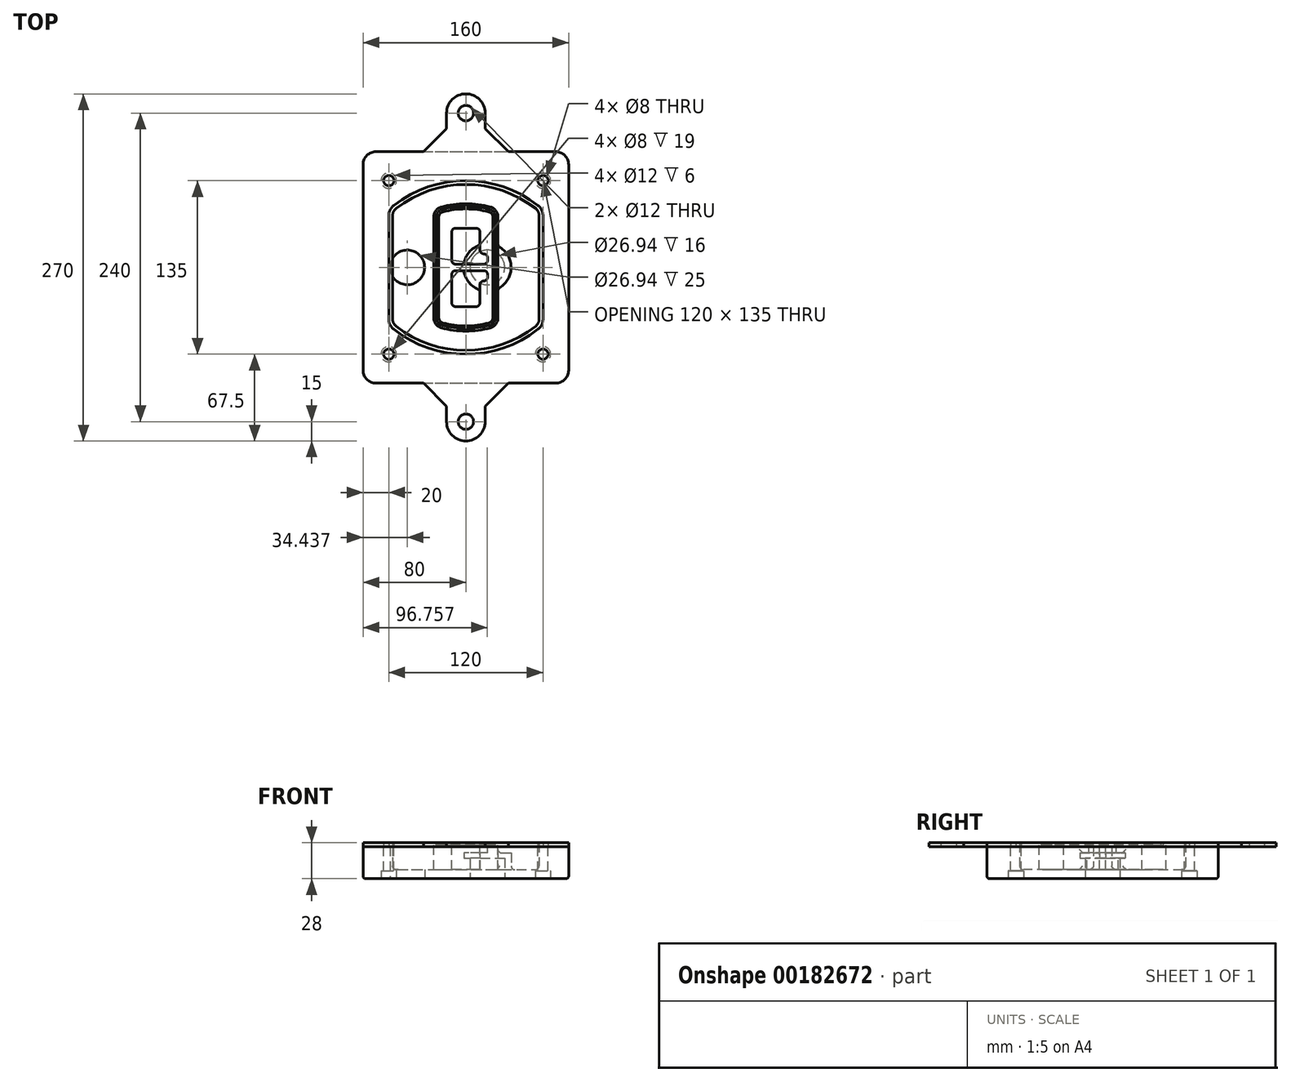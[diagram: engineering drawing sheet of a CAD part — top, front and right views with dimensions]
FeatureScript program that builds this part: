
annotation { "Feature Type Name" : "Feature", "Feature Type Description" : "" }
export const myFeature = defineFeature(function(context is Context, id is Id, definition is map)
    precondition{}
    {
        {
            var Q0;
            Q0=qCreatedBy(makeId("Top.planeOp"),FACE);
            var sketch = newSketch(context, id + "F0", { "sketchPlane" : qUnion([Q0])});
            skPoint(sketch, "E0.rect.middle", {"position": v(0, 0) * mm});
            skLineSegment(sketch, "E1.bottom", {"start": v(-70, -90) * mm, "end": v(70, -90) * mm});
            skLineSegment(sketch, "E1.top", {"start": v(-70, 90) * mm, "end": v(70, 90) * mm});
            skLineSegment(sketch, "E1.left", {"start": v(-80, -80) * mm, "end": v(-80, 80) * mm});
            skLineSegment(sketch, "E1.right", {"start": v(80, -80) * mm, "end": v(80, 80) * mm});
            skLineSegment(sketch, "E2", {"start": v(-80, 90) * mm, "end": v(80, -90) * mm, "construction": true});
            skLineSegment(sketch, "E3", {"start": v(80, 90) * mm, "end": v(-80, -90) * mm, "construction": true});
            skCircle(sketch, "E4", {"center": v(-60, 67.5) * mm, "radius": 4 * mm});
            skCircle(sketch, "E5", {"center": v(60, 67.5) * mm, "radius": 4 * mm});
            skCircle(sketch, "E6", {"center": v(60, -67.5) * mm, "radius": 4 * mm});
            skCircle(sketch, "E7", {"center": v(-60, -67.5) * mm, "radius": 4 * mm});
            skLineSegment(sketch, "E8", {"start": v(-60, 67.5) * mm, "end": v(60, 67.5) * mm, "construction": true});
            skLineSegment(sketch, "E9", {"start": v(60, 67.5) * mm, "end": v(60, -67.5) * mm, "construction": true});
            skLineSegment(sketch, "E10", {"start": v(60, -67.5) * mm, "end": v(-60, -67.5) * mm, "construction": true});
            skLineSegment(sketch, "E11", {"start": v(-60, -67.5) * mm, "end": v(-60, 67.5) * mm, "construction": true});
            skLineSegment(sketch, "E12", {"start": v(-60, 40.3) * mm, "end": v(-60, -40.3) * mm});
            skLineSegment(sketch, "E13", {"start": v(60, 40.3) * mm, "end": v(60, -40.3) * mm});
            skArc(sketch, "E14", {"start": v(56.15, 48.18) * mm, "mid": v(0, 67.5) * mm, "end": v(-56.15, 48.18) * mm});
            skArc(sketch, "E15", {"start": v(-56.15, -48.18) * mm, "mid": v(0, -67.5) * mm, "end": v(56.15, -48.18) * mm});
            skLineSegment(sketch, "E16", {"start": v(-60, 0) * mm, "end": v(60, 0) * mm, "construction": true});
            skPoint(sketch, "E17.visualSharp", {"position": v(-60, -45) * mm});
            skArc(sketch, "E17.filletArc", {"start": v(-60, -40.3) * mm, "mid": v(-58.99, -44.68) * mm, "end": v(-56.15, -48.18) * mm});
            skPoint(sketch, "E18.visualSharp", {"position": v(-60, 45) * mm});
            skArc(sketch, "E18.filletArc", {"start": v(-56.15, 48.18) * mm, "mid": v(-58.99, 44.68) * mm, "end": v(-60, 40.3) * mm});
            skPoint(sketch, "E19.visualSharp", {"position": v(60, 45) * mm});
            skArc(sketch, "E19.filletArc", {"start": v(60, 40.3) * mm, "mid": v(58.99, 44.68) * mm, "end": v(56.15, 48.18) * mm});
            skPoint(sketch, "E20.visualSharp", {"position": v(60, -45) * mm});
            skArc(sketch, "E20.filletArc", {"start": v(56.15, -48.18) * mm, "mid": v(58.99, -44.68) * mm, "end": v(60, -40.3) * mm});
            skPoint(sketch, "E21.visualSharp", {"position": v(-80, 90) * mm});
            skArc(sketch, "E21.filletArc", {"start": v(-70, 90) * mm, "mid": v(-77.07, 87.07) * mm, "end": v(-80, 80) * mm});
            skPoint(sketch, "E22.visualSharp", {"position": v(80, 90) * mm});
            skArc(sketch, "E22.filletArc", {"start": v(80, 80) * mm, "mid": v(77.07, 87.07) * mm, "end": v(70, 90) * mm});
            skPoint(sketch, "E23.visualSharp", {"position": v(80, -90) * mm});
            skArc(sketch, "E23.filletArc", {"start": v(70, -90) * mm, "mid": v(77.07, -87.07) * mm, "end": v(80, -80) * mm});
            skPoint(sketch, "E24.visualSharp", {"position": v(-80, -90) * mm});
            skArc(sketch, "E24.filletArc", {"start": v(-80, -80) * mm, "mid": v(-77.07, -87.07) * mm, "end": v(-70, -90) * mm});
            skArc(sketch, "E25.0", {"start": v(57, 40.3) * mm, "mid": v(56.3, 43.36) * mm, "end": v(54.3, 45.81) * mm});
            skLineSegment(sketch, "E25.1", {"start": v(57, 40.3) * mm, "end": v(57, -40.3) * mm});
            skArc(sketch, "E25.2", {"start": v(54.3, -45.81) * mm, "mid": v(56.3, -43.36) * mm, "end": v(57, -40.3) * mm});
            skArc(sketch, "E25.3", {"start": v(-54.3, -45.81) * mm, "mid": v(0, -64.5) * mm, "end": v(54.3, -45.81) * mm});
            skArc(sketch, "E25.4", {"start": v(-57, -40.3) * mm, "mid": v(-56.3, -43.36) * mm, "end": v(-54.3, -45.81) * mm});
            skArc(sketch, "E25.5", {"start": v(54.3, 45.81) * mm, "mid": v(0, 64.5) * mm, "end": v(-54.3, 45.81) * mm});
            skLineSegment(sketch, "E25.6", {"start": v(-57, 40.3) * mm, "end": v(-57, -40.3) * mm});
            skArc(sketch, "E25.7", {"start": v(-54.3, 45.81) * mm, "mid": v(-56.3, 43.36) * mm, "end": v(-57, 40.3) * mm});
            skArc(sketch, "E26.0", {"start": v(-58.62, 51.33) * mm, "mid": v(-62.58, 46.43) * mm, "end": v(-64, 40.3) * mm});
            skArc(sketch, "E26.1", {"start": v(58.62, 51.33) * mm, "mid": v(0, 71.5) * mm, "end": v(-58.62, 51.33) * mm});
            skArc(sketch, "E26.2", {"start": v(64, 40.3) * mm, "mid": v(62.58, 46.43) * mm, "end": v(58.62, 51.33) * mm});
            skLineSegment(sketch, "E26.3", {"start": v(64, 40.3) * mm, "end": v(64, -40.3) * mm});
            skArc(sketch, "E26.4", {"start": v(58.62, -51.33) * mm, "mid": v(62.58, -46.43) * mm, "end": v(64, -40.3) * mm});
            skLineSegment(sketch, "E26.5", {"start": v(-64, 40.3) * mm, "end": v(-64, -40.3) * mm});
            skArc(sketch, "E26.6", {"start": v(-58.62, -51.33) * mm, "mid": v(0, -71.5) * mm, "end": v(58.62, -51.33) * mm});
            skArc(sketch, "E26.7", {"start": v(-64, -40.3) * mm, "mid": v(-62.58, -46.43) * mm, "end": v(-58.62, -51.33) * mm});
            skSolve(sketch);
        }
        {
            var Q0;
            Q0=makeQuery(id+"F0.imprint","IMPRINT",FACE,{"disambiguationData":[TD([[makeQuery(id+"F0.imprint","IMPRINT",EDGE,{"derivedFrom":sQuery(id+"F0.wireOp",EDGE,"E1.bottom")}),1.0]])]});
            var Q1;
            Q1=makeQuery(id+"F0.imprint","IMPRINT",FACE,{"disambiguationData":[TD([[makeQuery(id+"F0.imprint","IMPRINT",EDGE,{"derivedFrom":sQuery(id+"F0.wireOp",EDGE,"E12")}),1.0]])]});
            var Q2;
            Q2=makeQuery(id+"F0.imprint","IMPRINT",FACE,{"disambiguationData":[TD([[makeQuery(id+"F0.imprint","IMPRINT",EDGE,{"derivedFrom":sQuery(id+"F0.wireOp",EDGE,"E25.0")}),1.0]])]});
            var Q3;
            Q3=makeQuery(id+"F0.imprint","IMPRINT",FACE,{"disambiguationData":[TD([[makeQuery(id+"F0.imprint","IMPRINT",EDGE,{"derivedFrom":sQuery(id+"F0.wireOp",EDGE,"E12")}),-1.0]])]});
            extrude(context, id + "F1", {"entities" : qUnion([Q0, Q1, Q2, Q3]), "oppositeDirection" : true, "depth" : 25 * mm});
        }
        {
            var Q0;
            Q0=makeQuery(id+"F0.imprint","IMPRINT",FACE,{"disambiguationData":[TD([[makeQuery(id+"F0.imprint","IMPRINT",EDGE,{"derivedFrom":sQuery(id+"F0.wireOp",EDGE,"E12")}),1.0]])]});
            extrude(context, id + "F2", {"entities" : qUnion([Q0]), "operationType" : NewBodyOperationType.ADD, "depth" : 3 * mm});
        }
        {
            var Q0;
            Q0=makeQuery(id+"F0.imprint","IMPRINT",FACE,{"disambiguationData":[TD([[makeQuery(id+"F0.imprint","IMPRINT",EDGE,{"derivedFrom":sQuery(id+"F0.wireOp",EDGE,"E25.0")}),1.0]])]});
            extrude(context, id + "F3", {"entities" : qUnion([Q0]), "operationType" : NewBodyOperationType.REMOVE, "oppositeDirection" : true, "depth" : 18 * mm});
        }
        {
            var Q0;
            Q0=makeQuery(id+"F2.opExtrude","CAP_FACE",FACE,{"disambiguationData":[OSD([sQuery(id+"F0.wireOp",EDGE,"E12"),sQuery(id+"F0.wireOp",EDGE,"E13"),sQuery(id+"F0.wireOp",EDGE,"E14"),sQuery(id+"F0.wireOp",EDGE,"E15"),sQuery(id+"F0.wireOp",EDGE,"E17.filletArc"),sQuery(id+"F0.wireOp",EDGE,"E18.filletArc"),sQuery(id+"F0.wireOp",EDGE,"E19.filletArc"),sQuery(id+"F0.wireOp",EDGE,"E20.filletArc"),sQuery(id+"F0.wireOp",EDGE,"E25.0"),sQuery(id+"F0.wireOp",EDGE,"E25.1"),sQuery(id+"F0.wireOp",EDGE,"E25.2"),sQuery(id+"F0.wireOp",EDGE,"E25.3"),sQuery(id+"F0.wireOp",EDGE,"E25.4"),sQuery(id+"F0.wireOp",EDGE,"E25.5"),sQuery(id+"F0.wireOp",EDGE,"E25.6"),sQuery(id+"F0.wireOp",EDGE,"E25.7")])],"isStart":false});
            var sketch = newSketch(context, id + "F4", { "sketchPlane" : qUnion([Q0])});
            skArc(sketch, "E27.0", {"start": v(-19.08, -46.97) * mm, "mid": v(0, -49.5) * mm, "end": v(19.08, -46.97) * mm});
            skArc(sketch, "E28.0", {"start": v(19.08, 46.97) * mm, "mid": v(0, 49.5) * mm, "end": v(-19.08, 46.97) * mm});
            skLineSegment(sketch, "E29", {"start": v(-25, 39.25) * mm, "end": v(-25, -39.25) * mm});
            skLineSegment(sketch, "E30", {"start": v(25, 39.25) * mm, "end": v(25, -39.25) * mm});
            skLineSegment(sketch, "E31", {"start": v(-25, 45.1) * mm, "end": v(25, 45.1) * mm, "construction": true});
            skLineSegment(sketch, "E32", {"start": v(-25, -45.1) * mm, "end": v(25, -45.1) * mm, "construction": true});
            skPoint(sketch, "E33.visualSharp", {"position": v(-25, 45.1) * mm});
            skArc(sketch, "E33.filletArc", {"start": v(-19.08, 46.97) * mm, "mid": v(-23.35, 44.11) * mm, "end": v(-25, 39.25) * mm});
            skPoint(sketch, "E34.visualSharp", {"position": v(25, 45.1) * mm});
            skArc(sketch, "E34.filletArc", {"start": v(25, 39.25) * mm, "mid": v(23.35, 44.11) * mm, "end": v(19.08, 46.97) * mm});
            skPoint(sketch, "E35.visualSharp", {"position": v(25, -45.1) * mm});
            skArc(sketch, "E35.filletArc", {"start": v(19.08, -46.97) * mm, "mid": v(23.35, -44.11) * mm, "end": v(25, -39.25) * mm});
            skPoint(sketch, "E36.visualSharp", {"position": v(-25, -45.1) * mm});
            skArc(sketch, "E36.filletArc", {"start": v(-25, -39.25) * mm, "mid": v(-23.35, -44.11) * mm, "end": v(-19.08, -46.97) * mm});
            skArc(sketch, "E37.0", {"start": v(54.3, 45.81) * mm, "mid": v(0, 64.5) * mm, "end": v(-54.3, 45.81) * mm});
            skArc(sketch, "E37.1", {"start": v(-54.3, 45.81) * mm, "mid": v(-56.3, 43.36) * mm, "end": v(-57, 40.3) * mm});
            skLineSegment(sketch, "E37.2", {"start": v(-57, 40.3) * mm, "end": v(-57, -40.3) * mm});
            skArc(sketch, "E37.3", {"start": v(-57, -40.3) * mm, "mid": v(-56.3, -43.36) * mm, "end": v(-54.3, -45.81) * mm});
            skArc(sketch, "E37.4", {"start": v(-54.3, -45.81) * mm, "mid": v(0, -64.5) * mm, "end": v(54.3, -45.81) * mm});
            skArc(sketch, "E37.5", {"start": v(54.3, -45.81) * mm, "mid": v(56.3, -43.36) * mm, "end": v(57, -40.3) * mm});
            skLineSegment(sketch, "E37.6", {"start": v(57, 40.3) * mm, "end": v(57, -40.3) * mm});
            skArc(sketch, "E37.7", {"start": v(57, 40.3) * mm, "mid": v(56.3, 43.36) * mm, "end": v(54.3, 45.81) * mm});
            skLineSegment(sketch, "E38.0", {"start": v(23, 39.25) * mm, "end": v(23, -39.25) * mm});
            skArc(sketch, "E38.1", {"start": v(18.56, -45.04) * mm, "mid": v(21.76, -42.9) * mm, "end": v(23, -39.25) * mm});
            skArc(sketch, "E38.2", {"start": v(-18.56, -45.04) * mm, "mid": v(0, -47.5) * mm, "end": v(18.56, -45.04) * mm});
            skArc(sketch, "E38.3", {"start": v(-23, -39.25) * mm, "mid": v(-21.76, -42.9) * mm, "end": v(-18.56, -45.04) * mm});
            skLineSegment(sketch, "E38.4", {"start": v(-23, 39.25) * mm, "end": v(-23, -39.25) * mm});
            skArc(sketch, "E38.5", {"start": v(23, 39.25) * mm, "mid": v(21.76, 42.9) * mm, "end": v(18.56, 45.04) * mm});
            skArc(sketch, "E38.6", {"start": v(-18.56, 45.04) * mm, "mid": v(-21.76, 42.9) * mm, "end": v(-23, 39.25) * mm});
            skArc(sketch, "E38.7", {"start": v(18.56, 45.04) * mm, "mid": v(0, 47.5) * mm, "end": v(-18.56, 45.04) * mm});
            skArc(sketch, "E39.0", {"start": v(21, 39.25) * mm, "mid": v(20.18, 41.68) * mm, "end": v(18.04, 43.1) * mm});
            skLineSegment(sketch, "E39.1", {"start": v(21, 39.25) * mm, "end": v(21, -39.25) * mm});
            skArc(sketch, "E39.2", {"start": v(18.04, -43.1) * mm, "mid": v(20.18, -41.68) * mm, "end": v(21, -39.25) * mm});
            skArc(sketch, "E39.3", {"start": v(-18.04, -43.1) * mm, "mid": v(0, -45.5) * mm, "end": v(18.04, -43.1) * mm});
            skArc(sketch, "E39.4", {"start": v(-21, -39.25) * mm, "mid": v(-20.18, -41.68) * mm, "end": v(-18.04, -43.1) * mm});
            skArc(sketch, "E39.5", {"start": v(18.04, 43.1) * mm, "mid": v(0, 45.5) * mm, "end": v(-18.04, 43.1) * mm});
            skLineSegment(sketch, "E39.6", {"start": v(-21, 39.25) * mm, "end": v(-21, -39.25) * mm});
            skArc(sketch, "E39.7", {"start": v(-18.04, 43.1) * mm, "mid": v(-20.18, 41.68) * mm, "end": v(-21, 39.25) * mm});
            skLineSegment(sketch, "E40", {"start": v(-25, 0) * mm, "end": v(25, 0) * mm, "construction": true});
            skLineSegment(sketch, "E41", {"start": v(-11, 5.5) * mm, "end": v(-11, 27.5) * mm});
            skLineSegment(sketch, "E42", {"start": v(-8, 30.5) * mm, "end": v(8, 30.5) * mm});
            skLineSegment(sketch, "E43", {"start": v(11, 27.5) * mm, "end": v(11, 13.5) * mm});
            skLineSegment(sketch, "E44", {"start": v(14, 10.5) * mm, "end": v(14, 10.5) * mm});
            skLineSegment(sketch, "E45", {"start": v(17, 7.5) * mm, "end": v(17, 5.5) * mm});
            skLineSegment(sketch, "E46", {"start": v(14, 2.5) * mm, "end": v(-8, 2.5) * mm});
            skPoint(sketch, "E47.visualSharp", {"position": v(-11, 30.5) * mm});
            skArc(sketch, "E47.filletArc", {"start": v(-8, 30.5) * mm, "mid": v(-10.12, 29.62) * mm, "end": v(-11, 27.5) * mm});
            skPoint(sketch, "E48.visualSharp", {"position": v(11, 30.5) * mm});
            skArc(sketch, "E48.filletArc", {"start": v(11, 27.5) * mm, "mid": v(10.12, 29.62) * mm, "end": v(8, 30.5) * mm});
            skPoint(sketch, "E49.visualSharp", {"position": v(11, 10.5) * mm});
            skArc(sketch, "E49.filletArc", {"start": v(11, 13.5) * mm, "mid": v(11.88, 11.38) * mm, "end": v(14, 10.5) * mm});
            skPoint(sketch, "E50.visualSharp", {"position": v(17, 10.5) * mm});
            skArc(sketch, "E50.filletArc", {"start": v(17, 7.5) * mm, "mid": v(16.12, 9.62) * mm, "end": v(14, 10.5) * mm});
            skPoint(sketch, "E51.visualSharp", {"position": v(17, 2.5) * mm});
            skArc(sketch, "E51.filletArc", {"start": v(14, 2.5) * mm, "mid": v(16.12, 3.38) * mm, "end": v(17, 5.5) * mm});
            skPoint(sketch, "E52.visualSharp", {"position": v(-11, 2.5) * mm});
            skArc(sketch, "E52.filletArc", {"start": v(-11, 5.5) * mm, "mid": v(-10.12, 3.38) * mm, "end": v(-8, 2.5) * mm});
            skLineSegment(sketch, "E53.0.MirrorCS", {"start": v(14, -2.5) * mm, "end": v(-8, -2.5) * mm});
            skArc(sketch, "E54.0.MirrorCS", {"start": v(-11, -5.5) * mm, "mid": v(-10.12, -3.38) * mm, "end": v(-8, -2.5) * mm});
            skLineSegment(sketch, "E55.0.MirrorCS", {"start": v(-11, -5.5) * mm, "end": v(-11, -27.5) * mm});
            skArc(sketch, "E56.0.MirrorCS", {"start": v(-8, -30.5) * mm, "mid": v(-10.12, -29.62) * mm, "end": v(-11, -27.5) * mm});
            skLineSegment(sketch, "E57.0.MirrorCS", {"start": v(-8, -30.5) * mm, "end": v(8, -30.5) * mm});
            skArc(sketch, "E58.0.MirrorCS", {"start": v(11, -27.5) * mm, "mid": v(10.12, -29.62) * mm, "end": v(8, -30.5) * mm});
            skLineSegment(sketch, "E59.0.MirrorCS", {"start": v(11, -27.5) * mm, "end": v(11, -13.5) * mm});
            skArc(sketch, "E60.0.MirrorCS", {"start": v(11, -13.5) * mm, "mid": v(11.88, -11.38) * mm, "end": v(14, -10.5) * mm});
            skArc(sketch, "E61.0.MirrorCS", {"start": v(17, -7.5) * mm, "mid": v(16.12, -9.62) * mm, "end": v(14, -10.5) * mm});
            skLineSegment(sketch, "E62.0.MirrorCS", {"start": v(17, -7.5) * mm, "end": v(17, -5.5) * mm});
            skArc(sketch, "E63.0.MirrorCS", {"start": v(14, -2.5) * mm, "mid": v(16.12, -3.38) * mm, "end": v(17, -5.5) * mm});
            skSolve(sketch);
        }
        {
            var Q0;
            Q0=makeQuery(id+"F4.imprint","IMPRINT",FACE,{"disambiguationData":[TD([[makeQuery(id+"F4.imprint","IMPRINT",EDGE,{"derivedFrom":sQuery(id+"F4.wireOp",EDGE,"E27.0")}),1.0]])]});
            var Q1;
            Q1=makeQuery(id+"F4.imprint","IMPRINT",FACE,{"disambiguationData":[TD([[makeQuery(id+"F4.imprint","IMPRINT",EDGE,{"derivedFrom":sQuery(id+"F4.wireOp",EDGE,"E38.0")}),-1.0]])]});
            var Q2;
            Q2=makeQuery(id+"F4.imprint","IMPRINT",FACE,{"disambiguationData":[TD([[makeQuery(id+"F4.imprint","IMPRINT",EDGE,{"derivedFrom":sQuery(id+"F4.wireOp",EDGE,"E39.0")}),1.0]])]});
            extrude(context, id + "F5", {"entities" : qUnion([Q0, Q1, Q2]), "operationType" : NewBodyOperationType.ADD, "endBound" : BoundingType.UP_TO_NEXT, "oppositeDirection" : true, "depth" : 25 * mm});
        }
        {
            var Q0;
            Q0=makeQuery(id+"F4.imprint","IMPRINT",FACE,{"disambiguationData":[TD([[makeQuery(id+"F4.imprint","IMPRINT",EDGE,{"derivedFrom":sQuery(id+"F4.wireOp",EDGE,"E38.0")}),-1.0]])]});
            extrude(context, id + "F6", {"entities" : qUnion([Q0]), "operationType" : NewBodyOperationType.REMOVE, "oppositeDirection" : true, "depth" : 2 * mm});
        }
        {
            var Q0;
            Q0=makeQuery(id+"F1.opExtrude","CAP_FACE",FACE,{"disambiguationData":[OSD([sQuery(id+"F0.wireOp",EDGE,"E1.bottom"),sQuery(id+"F0.wireOp",EDGE,"E1.top"),sQuery(id+"F0.wireOp",EDGE,"E1.left"),sQuery(id+"F0.wireOp",EDGE,"E1.right"),sQuery(id+"F0.wireOp",EDGE,"E4"),sQuery(id+"F0.wireOp",EDGE,"E5"),sQuery(id+"F0.wireOp",EDGE,"E6"),sQuery(id+"F0.wireOp",EDGE,"E7"),sQuery(id+"F0.wireOp",EDGE,"E21.filletArc"),sQuery(id+"F0.wireOp",EDGE,"E22.filletArc"),sQuery(id+"F0.wireOp",EDGE,"E23.filletArc"),sQuery(id+"F0.wireOp",EDGE,"E24.filletArc")])],"isStart":false});
            var sketch = newSketch(context, id + "F7", { "sketchPlane" : qUnion([Q0])});
            skCircle(sketch, "E64", {"center": v(16.76, 0) * mm, "radius": 13.47 * mm});
            skCircle(sketch, "E65", {"center": v(-45.56, 0) * mm, "radius": 13.47 * mm});
            skLineSegment(sketch, "E66", {"start": v(80, 0) * mm, "end": v(-80, 0) * mm});
            skCircle(sketch, "E67", {"center": v(16.76, 0) * mm, "radius": 18.47 * mm});
            skCircle(sketch, "E68", {"center": v(60, -67.5) * mm, "radius": 6 * mm});
            skCircle(sketch, "E69", {"center": v(-60, -67.5) * mm, "radius": 6 * mm});
            skCircle(sketch, "E70", {"center": v(-60, 67.5) * mm, "radius": 6 * mm});
            skCircle(sketch, "E71", {"center": v(60, 67.5) * mm, "radius": 6 * mm});
            skSolve(sketch);
        }
        {
            var Q0;
            {var subQ1=sQuery(id+"F7.wireOp",EDGE,"E66");var subQ4=sQuery(id+"F7.wireOp",EDGE,"E64");var subQ6=makeQuery(id+"F7.imprint","INTERSECT",VERTEX,{"disambiguationData":[OD(0.0)],"derivedFrom":[subQ4,subQ1]});Q0=makeQuery(id+"F7.imprint","IMPRINT",FACE,{"disambiguationData":[TD([[makeQuery(id+"F7.imprint","IMPRINT",EDGE,{"disambiguationData":[TD([[subQ6,-1.0]])],"derivedFrom":subQ4}),-1.0]])]});}
            var Q1;
            {var subQ0=sQuery(id+"F7.wireOp",EDGE,"E66");var subQ1=sQuery(id+"F7.wireOp",EDGE,"E64");var subQ3=makeQuery(id+"F7.imprint","INTERSECT",VERTEX,{"disambiguationData":[OD(0.0)],"derivedFrom":[subQ1,subQ0]});Q1=makeQuery(id+"F7.imprint","IMPRINT",FACE,{"disambiguationData":[TD([[makeQuery(id+"F7.imprint","IMPRINT",EDGE,{"disambiguationData":[TD([[subQ3,-1.0]])],"derivedFrom":subQ1}),1.0]])]});}
            var Q2;
            {var subQ0=sQuery(id+"F7.wireOp",EDGE,"E66");var subQ1=sQuery(id+"F7.wireOp",EDGE,"E64");var subQ3=makeQuery(id+"F7.imprint","INTERSECT",VERTEX,{"disambiguationData":[OD(0.0)],"derivedFrom":[subQ1,subQ0]});Q2=makeQuery(id+"F7.imprint","IMPRINT",FACE,{"disambiguationData":[TD([[makeQuery(id+"F7.imprint","IMPRINT",EDGE,{"disambiguationData":[TD([[subQ3,1.0]])],"derivedFrom":subQ1}),1.0]])]});}
            var Q3;
            {var subQ1=sQuery(id+"F7.wireOp",EDGE,"E66");var subQ4=sQuery(id+"F7.wireOp",EDGE,"E64");var subQ6=makeQuery(id+"F7.imprint","INTERSECT",VERTEX,{"disambiguationData":[OD(0.0)],"derivedFrom":[subQ4,subQ1]});Q3=makeQuery(id+"F7.imprint","IMPRINT",FACE,{"disambiguationData":[TD([[makeQuery(id+"F7.imprint","IMPRINT",EDGE,{"disambiguationData":[TD([[subQ6,1.0]])],"derivedFrom":subQ4}),-1.0]])]});}
            extrude(context, id + "F8", {"entities" : qUnion([Q0, Q1, Q2, Q3]), "operationType" : NewBodyOperationType.ADD, "oppositeDirection" : true, "depth" : 20 * mm});
        }
        {
            var Q0;
            {var subQ0=sQuery(id+"F7.wireOp",EDGE,"E66");var subQ1=sQuery(id+"F7.wireOp",EDGE,"E64");var subQ3=makeQuery(id+"F7.imprint","INTERSECT",VERTEX,{"disambiguationData":[OD(0.0)],"derivedFrom":[subQ1,subQ0]});Q0=makeQuery(id+"F7.imprint","IMPRINT",FACE,{"disambiguationData":[TD([[makeQuery(id+"F7.imprint","IMPRINT",EDGE,{"disambiguationData":[TD([[subQ3,-1.0]])],"derivedFrom":subQ1}),1.0]])]});}
            var Q1;
            {var subQ0=sQuery(id+"F7.wireOp",EDGE,"E66");var subQ1=sQuery(id+"F7.wireOp",EDGE,"E64");var subQ3=makeQuery(id+"F7.imprint","INTERSECT",VERTEX,{"disambiguationData":[OD(0.0)],"derivedFrom":[subQ1,subQ0]});Q1=makeQuery(id+"F7.imprint","IMPRINT",FACE,{"disambiguationData":[TD([[makeQuery(id+"F7.imprint","IMPRINT",EDGE,{"disambiguationData":[TD([[subQ3,1.0]])],"derivedFrom":subQ1}),1.0]])]});}
            extrude(context, id + "F9", {"entities" : qUnion([Q0, Q1]), "operationType" : NewBodyOperationType.REMOVE, "oppositeDirection" : true, "depth" : 16 * mm});
        }
        {
            var Q0;
            {var subQ0=sQuery(id+"F7.wireOp",EDGE,"E66");var subQ1=sQuery(id+"F7.wireOp",EDGE,"E65");var subQ3=makeQuery(id+"F7.imprint","INTERSECT",VERTEX,{"disambiguationData":[OD(0.0)],"derivedFrom":[subQ1,subQ0]});Q0=makeQuery(id+"F7.imprint","IMPRINT",FACE,{"disambiguationData":[TD([[makeQuery(id+"F7.imprint","IMPRINT",EDGE,{"disambiguationData":[TD([[subQ3,-1.0]])],"derivedFrom":subQ1}),1.0]])]});}
            var Q1;
            {var subQ0=sQuery(id+"F7.wireOp",EDGE,"E66");var subQ1=sQuery(id+"F7.wireOp",EDGE,"E65");var subQ3=makeQuery(id+"F7.imprint","INTERSECT",VERTEX,{"disambiguationData":[OD(0.0)],"derivedFrom":[subQ1,subQ0]});Q1=makeQuery(id+"F7.imprint","IMPRINT",FACE,{"disambiguationData":[TD([[makeQuery(id+"F7.imprint","IMPRINT",EDGE,{"disambiguationData":[TD([[subQ3,1.0]])],"derivedFrom":subQ1}),1.0]])]});}
            extrude(context, id + "F10", {"entities" : qUnion([Q0, Q1]), "operationType" : NewBodyOperationType.REMOVE, "oppositeDirection" : true, "depth" : 25 * mm});
        }
        {
            var Q0;
            Q0=makeQuery(id+"F7.imprint","IMPRINT",FACE,{"disambiguationData":[TD([[makeQuery(id+"F7.imprint","IMPRINT",EDGE,{"derivedFrom":sQuery(id+"F7.wireOp",EDGE,"E68")}),1.0]])]});
            var Q1;
            Q1=makeQuery(id+"F7.imprint","IMPRINT",FACE,{"disambiguationData":[TD([[makeQuery(id+"F7.imprint","IMPRINT",EDGE,{"derivedFrom":makeQuery(id+"F1.opExtrude","CAP_EDGE",EDGE,{"disambiguationData":[OSD([sQuery(id+"F0.wireOp",EDGE,"E5")])],"isStart":false})}),-1.0]])]});
            var Q2;
            Q2=makeQuery(id+"F7.imprint","IMPRINT",FACE,{"disambiguationData":[TD([[makeQuery(id+"F7.imprint","IMPRINT",EDGE,{"derivedFrom":sQuery(id+"F7.wireOp",EDGE,"E69")}),1.0]])]});
            var Q3;
            Q3=makeQuery(id+"F7.imprint","IMPRINT",FACE,{"disambiguationData":[TD([[makeQuery(id+"F7.imprint","IMPRINT",EDGE,{"derivedFrom":makeQuery(id+"F1.opExtrude","CAP_EDGE",EDGE,{"disambiguationData":[OSD([sQuery(id+"F0.wireOp",EDGE,"E4")])],"isStart":false})}),-1.0]])]});
            var Q4;
            Q4=makeQuery(id+"F7.imprint","IMPRINT",FACE,{"disambiguationData":[TD([[makeQuery(id+"F7.imprint","IMPRINT",EDGE,{"derivedFrom":sQuery(id+"F7.wireOp",EDGE,"E70")}),1.0]])]});
            var Q5;
            Q5=makeQuery(id+"F7.imprint","IMPRINT",FACE,{"disambiguationData":[TD([[makeQuery(id+"F7.imprint","IMPRINT",EDGE,{"derivedFrom":makeQuery(id+"F1.opExtrude","CAP_EDGE",EDGE,{"disambiguationData":[OSD([sQuery(id+"F0.wireOp",EDGE,"E7")])],"isStart":false})}),-1.0]])]});
            var Q6;
            Q6=makeQuery(id+"F7.imprint","IMPRINT",FACE,{"disambiguationData":[TD([[makeQuery(id+"F7.imprint","IMPRINT",EDGE,{"derivedFrom":sQuery(id+"F7.wireOp",EDGE,"E71")}),1.0]])]});
            var Q7;
            Q7=makeQuery(id+"F7.imprint","IMPRINT",FACE,{"disambiguationData":[TD([[makeQuery(id+"F7.imprint","IMPRINT",EDGE,{"derivedFrom":makeQuery(id+"F1.opExtrude","CAP_EDGE",EDGE,{"disambiguationData":[OSD([sQuery(id+"F0.wireOp",EDGE,"E6")])],"isStart":false})}),-1.0]])]});
            extrude(context, id + "F11", {"entities" : qUnion([Q0, Q1, Q2, Q3, Q4, Q5, Q6, Q7]), "operationType" : NewBodyOperationType.REMOVE, "oppositeDirection" : true, "depth" : 6 * mm});
        }
        {
            var Q0;
            Q0=makeQuery(id+"F9.boolean.opBoolean","COPY",FACE,{"derivedFrom":makeQuery(id+"F9.opExtrude","CAP_FACE",FACE,{"disambiguationData":[OSD([sQuery(id+"F7.wireOp",EDGE,"E64")])],"isStart":false})});
            var sketch = newSketch(context, id + "F12", { "sketchPlane" : qUnion([Q0])});
            skArc(sketch, "E72.0", {"start": v(11, 17.55) * mm, "mid": v(2.57, 11.82) * mm, "end": v(-1.54, 2.5) * mm});
            skArc(sketch, "E72.1", {"start": v(-1.54, -2.5) * mm, "mid": v(2.57, -11.82) * mm, "end": v(11, -17.55) * mm});
            skLineSegment(sketch, "E73", {"start": v(-1.54, -2.5) * mm, "end": v(14, -2.5) * mm});
            skLineSegment(sketch, "E74.0", {"start": v(14, 2.5) * mm, "end": v(-1.54, 2.5) * mm});
            skArc(sketch, "E74.1", {"start": v(14, 2.5) * mm, "mid": v(16.12, 3.38) * mm, "end": v(17, 5.5) * mm});
            skLineSegment(sketch, "E74.2", {"start": v(17, 7.5) * mm, "end": v(17, 5.5) * mm});
            skArc(sketch, "E74.3", {"start": v(17, 7.5) * mm, "mid": v(16.12, 9.62) * mm, "end": v(14, 10.5) * mm});
            skArc(sketch, "E74.4", {"start": v(11, 13.5) * mm, "mid": v(11.88, 11.38) * mm, "end": v(14, 10.5) * mm});
            skLineSegment(sketch, "E74.5", {"start": v(11, 17.55) * mm, "end": v(11, 13.5) * mm});
            skLineSegment(sketch, "E74.7", {"start": v(14, -2.5) * mm, "end": v(-1.54, -2.5) * mm});
            skArc(sketch, "E74.8", {"start": v(14, -2.5) * mm, "mid": v(16.12, -3.38) * mm, "end": v(17, -5.5) * mm});
            skLineSegment(sketch, "E74.9", {"start": v(17, -7.5) * mm, "end": v(17, -5.5) * mm});
            skArc(sketch, "E74.10", {"start": v(17, -7.5) * mm, "mid": v(16.12, -9.62) * mm, "end": v(14, -10.5) * mm});
            skArc(sketch, "E74.11", {"start": v(11, -13.5) * mm, "mid": v(11.88, -11.38) * mm, "end": v(14, -10.5) * mm});
            skLineSegment(sketch, "E74.12", {"start": v(11, -17.55) * mm, "end": v(11, -13.5) * mm});
            skPoint(sketch, "E75.orphan", {"position": v(11, -27.5) * mm});
            skPoint(sketch, "E76.orphan", {"position": v(-8, -2.5) * mm});
            skPoint(sketch, "E77.orphan", {"position": v(-8, 2.5) * mm});
            skPoint(sketch, "E78.orphan", {"position": v(11, 27.5) * mm});
            skSolve(sketch);
        }
        {
            var Q0;
            {var subQ7=sQuery(id+"F12.wireOp",EDGE,"E72.0");var subQ14=sQuery(id+"F12.wireOp",EDGE,"E72.1");var subQ16=sQuery(id+"F12.wireOp",EDGE,"E74.1");var subQ18=sQuery(id+"F12.wireOp",EDGE,"E74.8");Q0=qUnion([makeQuery(id+"F12.imprint","IMPRINT",FACE,{"disambiguationData":[TD([[makeQuery(id+"F12.imprint","IMPRINT",EDGE,{"derivedFrom":subQ7}),1.0]])]}),makeQuery(id+"F12.imprint","IMPRINT",FACE,{"disambiguationData":[TD([[makeQuery(id+"F12.imprint","IMPRINT",EDGE,{"derivedFrom":subQ14}),1.0]])]}),makeQuery(id+"F12.imprint","IMPRINT",FACE,{"disambiguationData":[TD([[makeQuery(id+"F12.imprint","IMPRINT",EDGE,{"derivedFrom":subQ16}),1.0]])]}),makeQuery(id+"F12.imprint","IMPRINT",FACE,{"disambiguationData":[TD([[makeQuery(id+"F12.imprint","IMPRINT",EDGE,{"derivedFrom":subQ18}),-1.0]])]})]);}
            var Q1;
            Q1=makeQuery(id+"F5.boolean.opBoolean","SPLIT",FACE,{"disambiguationData":[TD([makeQuery(id+"F5.opExtrude","SWEPT_FACE",FACE,{"disambiguationData":[OSD([sQuery(id+"F4.wireOp",EDGE,"E41")])]})])],"derivedFrom":makeQuery(id+"F3.boolean.opBoolean","COPY",FACE,{"derivedFrom":makeQuery(id+"F3.opExtrude","CAP_FACE",FACE,{"disambiguationData":[OSD([sQuery(id+"F0.wireOp",EDGE,"E25.0"),sQuery(id+"F0.wireOp",EDGE,"E25.1"),sQuery(id+"F0.wireOp",EDGE,"E25.2"),sQuery(id+"F0.wireOp",EDGE,"E25.3"),sQuery(id+"F0.wireOp",EDGE,"E25.4"),sQuery(id+"F0.wireOp",EDGE,"E25.5"),sQuery(id+"F0.wireOp",EDGE,"E25.6"),sQuery(id+"F0.wireOp",EDGE,"E25.7")])],"isStart":false})})});
            extrude(context, id + "F13", {"entities" : qUnion([Q0]), "operationType" : NewBodyOperationType.REMOVE, "endBound" : BoundingType.UP_TO_SURFACE, "endBoundEntityFace" : qUnion([Q1]), "depth" : 25 * mm});
        }
        {
            var Q0;
            Q0=makeQuery(id+"F3.boolean.opBoolean","COPY",EDGE,{"derivedFrom":makeQuery(id+"F3.opExtrude","CAP_EDGE",EDGE,{"disambiguationData":[OSD([sQuery(id+"F0.wireOp",EDGE,"E25.6")])],"isStart":false})});
            var Q1;
            Q1=makeQuery(id+"F8.boolean.opBoolean","INTERSECT",EDGE,{"derivedFrom":[makeQuery(id+"F5.opExtrude","SWEPT_FACE",FACE,{"disambiguationData":[OSD([sQuery(id+"F4.wireOp",EDGE,"E30")])]}),makeQuery(id+"F8.opExtrude","CAP_FACE",FACE,{"disambiguationData":[OSD([sQuery(id+"F7.wireOp",EDGE,"E67")])],"isStart":false})]});
            var Q2;
            Q2=makeQuery(id+"F8.boolean.opBoolean","INTERSECT",EDGE,{"disambiguationData":[OD(1.0)],"derivedFrom":[makeQuery(id+"F5.opExtrude","SWEPT_FACE",FACE,{"disambiguationData":[OSD([sQuery(id+"F4.wireOp",EDGE,"E30")])]}),makeQuery(id+"F8.opExtrude","SWEPT_FACE",FACE,{"disambiguationData":[OSD([sQuery(id+"F7.wireOp",EDGE,"E67")])]})]});
            var Q3;
            {var subQ0=sQuery(id+"F4.wireOp",EDGE,"E30");Q3=makeQuery(id+"F8.boolean.opBoolean","SPLIT",EDGE,{"disambiguationData":[TD([makeQuery(id+"F5.opExtrude","SWEPT_FACE",FACE,{"disambiguationData":[OSD([sQuery(id+"F4.wireOp",EDGE,"E35.filletArc")])]})])],"derivedFrom":makeQuery(id+"F5.opExtrude","CAP_EDGE",EDGE,{"disambiguationData":[OSD([subQ0])],"isStart":false})});}
            var Q4;
            {var subQ0=sQuery(id+"F0.wireOp",EDGE,"E25.7");var subQ1=sQuery(id+"F0.wireOp",EDGE,"E25.1");var subQ2=sQuery(id+"F0.wireOp",EDGE,"E25.6");var subQ3=sQuery(id+"F0.wireOp",EDGE,"E25.5");var subQ4=sQuery(id+"F0.wireOp",EDGE,"E25.4");var subQ5=sQuery(id+"F0.wireOp",EDGE,"E25.0");var subQ6=sQuery(id+"F0.wireOp",EDGE,"E25.2");var subQ7=sQuery(id+"F0.wireOp",EDGE,"E25.3");Q4=makeQuery(id+"F8.boolean.opBoolean","INTERSECT",EDGE,{"derivedFrom":[makeQuery(id+"F5.boolean.opBoolean","SPLIT",FACE,{"disambiguationData":[TD([makeQuery(id+"F2.opExtrude","SWEPT_FACE",FACE,{"disambiguationData":[OSD([subQ5])]})])],"derivedFrom":makeQuery(id+"F3.boolean.opBoolean","COPY",FACE,{"derivedFrom":makeQuery(id+"F3.opExtrude","CAP_FACE",FACE,{"disambiguationData":[OSD([subQ5,subQ1,subQ6,subQ7,subQ4,subQ3,subQ2,subQ0])],"isStart":false})})}),makeQuery(id+"F8.opExtrude","SWEPT_FACE",FACE,{"disambiguationData":[OSD([sQuery(id+"F7.wireOp",EDGE,"E67")])]})]});}
            var Q5;
            Q5=makeQuery(id+"F8.boolean.opBoolean","INTERSECT",EDGE,{"disambiguationData":[OD(0.0)],"derivedFrom":[makeQuery(id+"F5.opExtrude","SWEPT_FACE",FACE,{"disambiguationData":[OSD([sQuery(id+"F4.wireOp",EDGE,"E30")])]}),makeQuery(id+"F8.opExtrude","SWEPT_FACE",FACE,{"disambiguationData":[OSD([sQuery(id+"F7.wireOp",EDGE,"E67")])]})]});
            fillet(context, id + "F14", {"entities" : qUnion([Q0, Q1, Q2, Q3, Q4, Q5]), "radius" : 3 * mm, "tangentPropagation" : true, "allowEdgeOverflow" : false});
        }
        {
            var Q0;
            Q0=makeQuery(id+"F1.opExtrude","CAP_EDGE",EDGE,{"disambiguationData":[OSD([sQuery(id+"F0.wireOp",EDGE,"E1.bottom")])],"isStart":false});
            fillet(context, id + "F15", {"entities" : qUnion([Q0]), "radius" : 2 * mm, "tangentPropagation" : true, "allowEdgeOverflow" : false});
        }
        {
            var Q0;
            {var subQ0=sQuery(id+"F0.wireOp",EDGE,"E22.filletArc");var subQ1=sQuery(id+"F0.wireOp",EDGE,"E7");var subQ2=sQuery(id+"F0.wireOp",EDGE,"E6");var subQ3=sQuery(id+"F0.wireOp",EDGE,"E5");var subQ4=sQuery(id+"F0.wireOp",EDGE,"E4");var subQ5=sQuery(id+"F0.wireOp",EDGE,"E1.bottom");var subQ6=sQuery(id+"F0.wireOp",EDGE,"E21.filletArc");var subQ7=sQuery(id+"F0.wireOp",EDGE,"E1.top");var subQ8=sQuery(id+"F0.wireOp",EDGE,"E1.left");var subQ9=sQuery(id+"F0.wireOp",EDGE,"E1.right");var subQ10=sQuery(id+"F0.wireOp",EDGE,"E23.filletArc");var subQ11=sQuery(id+"F0.wireOp",EDGE,"E24.filletArc");Q0=makeQuery(id+"F2.boolean.opBoolean","SPLIT",FACE,{"disambiguationData":[TD([makeQuery(id+"F1.opExtrude","SWEPT_FACE",FACE,{"disambiguationData":[OSD([subQ5])]})])],"derivedFrom":makeQuery(id+"F1.opExtrude","CAP_FACE",FACE,{"disambiguationData":[OSD([subQ5,subQ7,subQ8,subQ9,subQ4,subQ3,subQ2,subQ1,subQ6,subQ0,subQ10,subQ11])],"isStart":true})});}
            var sketch = newSketch(context, id + "F16", { "sketchPlane" : qUnion([Q0])});
            skCircle(sketch, "E79.0", {"center": v(-60, 67.5) * mm, "radius": 4 * mm});
            skArc(sketch, "E79.1", {"start": v(56.15, 48.18) * mm, "mid": v(0, 67.5) * mm, "end": v(-56.15, 48.18) * mm});
            skArc(sketch, "E79.2", {"start": v(-56.15, 48.18) * mm, "mid": v(-58.99, 44.68) * mm, "end": v(-60, 40.3) * mm});
            skLineSegment(sketch, "E79.3", {"start": v(-60, 40.3) * mm, "end": v(-60, -40.3) * mm});
            skArc(sketch, "E79.4", {"start": v(-60, -40.3) * mm, "mid": v(-58.99, -44.68) * mm, "end": v(-56.15, -48.18) * mm});
            skArc(sketch, "E79.5", {"start": v(-56.15, -48.18) * mm, "mid": v(0, -67.5) * mm, "end": v(56.15, -48.18) * mm});
            skArc(sketch, "E79.6", {"start": v(56.15, -48.18) * mm, "mid": v(58.99, -44.68) * mm, "end": v(60, -40.3) * mm});
            skLineSegment(sketch, "E79.7", {"start": v(60, 40.3) * mm, "end": v(60, -40.3) * mm});
            skArc(sketch, "E79.8", {"start": v(60, 40.3) * mm, "mid": v(58.99, 44.68) * mm, "end": v(56.15, 48.18) * mm});
            skLineSegment(sketch, "E79.9", {"start": v(-70, 90) * mm, "end": v(70, 90) * mm});
            skArc(sketch, "E79.10", {"start": v(80, 80) * mm, "mid": v(77.07, 87.07) * mm, "end": v(70, 90) * mm});
            skArc(sketch, "E79.11", {"start": v(-70, 90) * mm, "mid": v(-77.07, 87.07) * mm, "end": v(-80, 80) * mm});
            skLineSegment(sketch, "E79.12", {"start": v(-80, -80) * mm, "end": v(-80, 80) * mm});
            skArc(sketch, "E79.13", {"start": v(-80, -80) * mm, "mid": v(-77.07, -87.07) * mm, "end": v(-70, -90) * mm});
            skLineSegment(sketch, "E79.14", {"start": v(-70, -90) * mm, "end": v(70, -90) * mm});
            skArc(sketch, "E79.15", {"start": v(70, -90) * mm, "mid": v(77.07, -87.07) * mm, "end": v(80, -80) * mm});
            skCircle(sketch, "E79.16", {"center": v(60, 67.5) * mm, "radius": 4 * mm});
            skCircle(sketch, "E79.17", {"center": v(60, -67.5) * mm, "radius": 4 * mm});
            skCircle(sketch, "E79.18", {"center": v(-60, -67.5) * mm, "radius": 4 * mm});
            skLineSegment(sketch, "E79.19", {"start": v(80, -80) * mm, "end": v(80, 80) * mm});
            skLineSegment(sketch, "E80", {"start": v(0, 90) * mm, "end": v(0, 120) * mm, "construction": true});
            skPoint(sketch, "E80.endSnap0", {"position": v(0, 90) * mm});
            skLineSegment(sketch, "E81", {"start": v(-33, 90) * mm, "end": v(-15, 108) * mm});
            skLineSegment(sketch, "E82", {"start": v(-15, 108) * mm, "end": v(-15, 120) * mm});
            skLineSegment(sketch, "E83", {"start": v(33, 90) * mm, "end": v(15, 108) * mm});
            skLineSegment(sketch, "E84", {"start": v(15, 108) * mm, "end": v(15, 120) * mm});
            skCircle(sketch, "E85", {"center": v(0, 120) * mm, "radius": 6 * mm});
            skArc(sketch, "E86", {"start": v(-15, 120) * mm, "mid": v(0, 135) * mm, "end": v(15, 120) * mm});
            skLineSegment(sketch, "E87", {"start": v(-80, 0) * mm, "end": v(80, 0) * mm, "construction": true});
            skLineSegment(sketch, "E88.MirrorCS", {"start": v(33, -90) * mm, "end": v(15, -108) * mm});
            skLineSegment(sketch, "E89.MirrorCS", {"start": v(0, -90) * mm, "end": v(0, -120) * mm, "construction": true});
            skLineSegment(sketch, "E90.MirrorCS", {"start": v(15, -108) * mm, "end": v(15, -120) * mm});
            skArc(sketch, "E91.MirrorCS", {"start": v(-15, -120) * mm, "mid": v(0, -135) * mm, "end": v(15, -120) * mm});
            skLineSegment(sketch, "E92.MirrorCS", {"start": v(-15, -108) * mm, "end": v(-15, -120) * mm});
            skLineSegment(sketch, "E93.MirrorCS", {"start": v(-33, -90) * mm, "end": v(-15, -108) * mm});
            skCircle(sketch, "E94.MirrorC", {"center": v(0, -120) * mm, "radius": 6 * mm});
            skSolve(sketch);
        }
        {
            var Q0;
            {var subQ1=sQuery(id+"F16.wireOp",EDGE,"E81");Q0=makeQuery(id+"F16.imprint","IMPRINT",FACE,{"disambiguationData":[TD([[makeQuery(id+"F16.imprint","IMPRINT",EDGE,{"derivedFrom":subQ1}),-1.0]])]});}
            var Q1;
            Q1=makeQuery(id+"F16.imprint","IMPRINT",FACE,{"disambiguationData":[TD([[makeQuery(id+"F16.imprint","IMPRINT",EDGE,{"derivedFrom":sQuery(id+"F16.wireOp",EDGE,"E79.0")}),-1.0]])]});
            var Q2;
            {var subQ0=sQuery(id+"F16.wireOp",EDGE,"E88.MirrorCS");Q2=makeQuery(id+"F16.imprint","IMPRINT",FACE,{"disambiguationData":[TD([[makeQuery(id+"F16.imprint","IMPRINT",EDGE,{"derivedFrom":subQ0}),-1.0]])]});}
            var Q3;
            Q3=makeQuery(id+"F2.opExtrude","CAP_FACE",FACE,{"disambiguationData":[OSD([sQuery(id+"F0.wireOp",EDGE,"E12"),sQuery(id+"F0.wireOp",EDGE,"E13"),sQuery(id+"F0.wireOp",EDGE,"E14"),sQuery(id+"F0.wireOp",EDGE,"E15"),sQuery(id+"F0.wireOp",EDGE,"E17.filletArc"),sQuery(id+"F0.wireOp",EDGE,"E18.filletArc"),sQuery(id+"F0.wireOp",EDGE,"E19.filletArc"),sQuery(id+"F0.wireOp",EDGE,"E20.filletArc"),sQuery(id+"F0.wireOp",EDGE,"E25.0"),sQuery(id+"F0.wireOp",EDGE,"E25.1"),sQuery(id+"F0.wireOp",EDGE,"E25.2"),sQuery(id+"F0.wireOp",EDGE,"E25.3"),sQuery(id+"F0.wireOp",EDGE,"E25.4"),sQuery(id+"F0.wireOp",EDGE,"E25.5"),sQuery(id+"F0.wireOp",EDGE,"E25.6"),sQuery(id+"F0.wireOp",EDGE,"E25.7")])],"isStart":false});
            extrude(context, id + "F17", {"entities" : qUnion([Q0, Q1, Q2]), "endBound" : BoundingType.UP_TO_SURFACE, "endBoundEntityFace" : qUnion([Q3]), "depth" : 25 * mm});
        }
    });
